# Revit family: Deca_Cuba de embutir-sobrepor retangular_Cubas Embutir-Sobrepor_L.1061
name_source: partatom
category: Plumbing Fixtures
units: mm (PartAtom-declared; Revit-internal decimal feet)

## family parameters
Cut with Voids When Loaded = Yes
Host = Face
Part Type = Normal
Room Calculation Point = No
Round Connector Dimension = Use Radius
Shared = No

## types (1)
- L.1061.17_Branco
    Acompanha o Produto = -
    Aprovado por = quattroD
    Atendimento ao Cliente = 0800-0117073
    Categoria = CUBAS
    Composição Anel Vedação = -
    Composição Assento = -
    Composição Básica = Argila, feldspato, caulim, vidrados e corantes inorgânicos.
    Composição Componente = Não Possui
    Comprimento do corte = 490 mm
    Consumo = -
    Cor Interna = -
    Cor Principal = Branco
    Cor Secundária = -
    Cores Componente = Não Possui
    Criado por = quattroD
    Código Pai = L.1061
    Default Elevation = 0 mm  [stored 0 ft]
    Description = Cuba de embutir/sobrepor retangular
    Diâmetro Ponto de Esgoto = 25 mm  [stored 0.082021 ft]
    Embutida = Yes
    Informações Complementares = -
    Itens de Instalação = 1601.C; 1601.C.CLI; 1602.C; 1602.C.PLA; 1680.C.100.112; 1682.C.100.112; 1684.C.100.112
    Largura do corte = 329 mm
    Linha = Cubas Embutir / Sobrepor
    Manufacturer = Deca
    Material = Deca_Branco
    Model = L.1061.17
    Norma = NBR-16728-1;NBR-16728-2
    Peso Líquido (Kg) = 13.593
    Pressão máx. funcionamento = -
    Pressão mín. Aquec. Acúmulo = -
    Pressão mín. Aquec. Passagem = -
    Pressão mín. funcionamento = -
    Raio Ponto de Esgoto = 13 mm
    Saída de Esgoto = Válvula Curta
    Segmento = Banheiro Luxo
    Sobreposta = No
    Tipo de dispositivo economizador = -
    Tipo de mecanismo utilizado = -
    Tipo de rosca de entrada = -
    Tipo de rosca de saída = -
    Type Comments = -
    URL = www.deca.com.br
    Vazão na Pressão máx. (L/min) = -
    Vazão na Pressão mín. (L/min) = -
    WFU = 0

note: [stored X ft] marks values corroborated as IEEE doubles in the binary element streams (Revit-internal decimal feet)

## geometry (parser evidence)
native form markers: Sweep x3
no freeform markers — native parametric forms only
